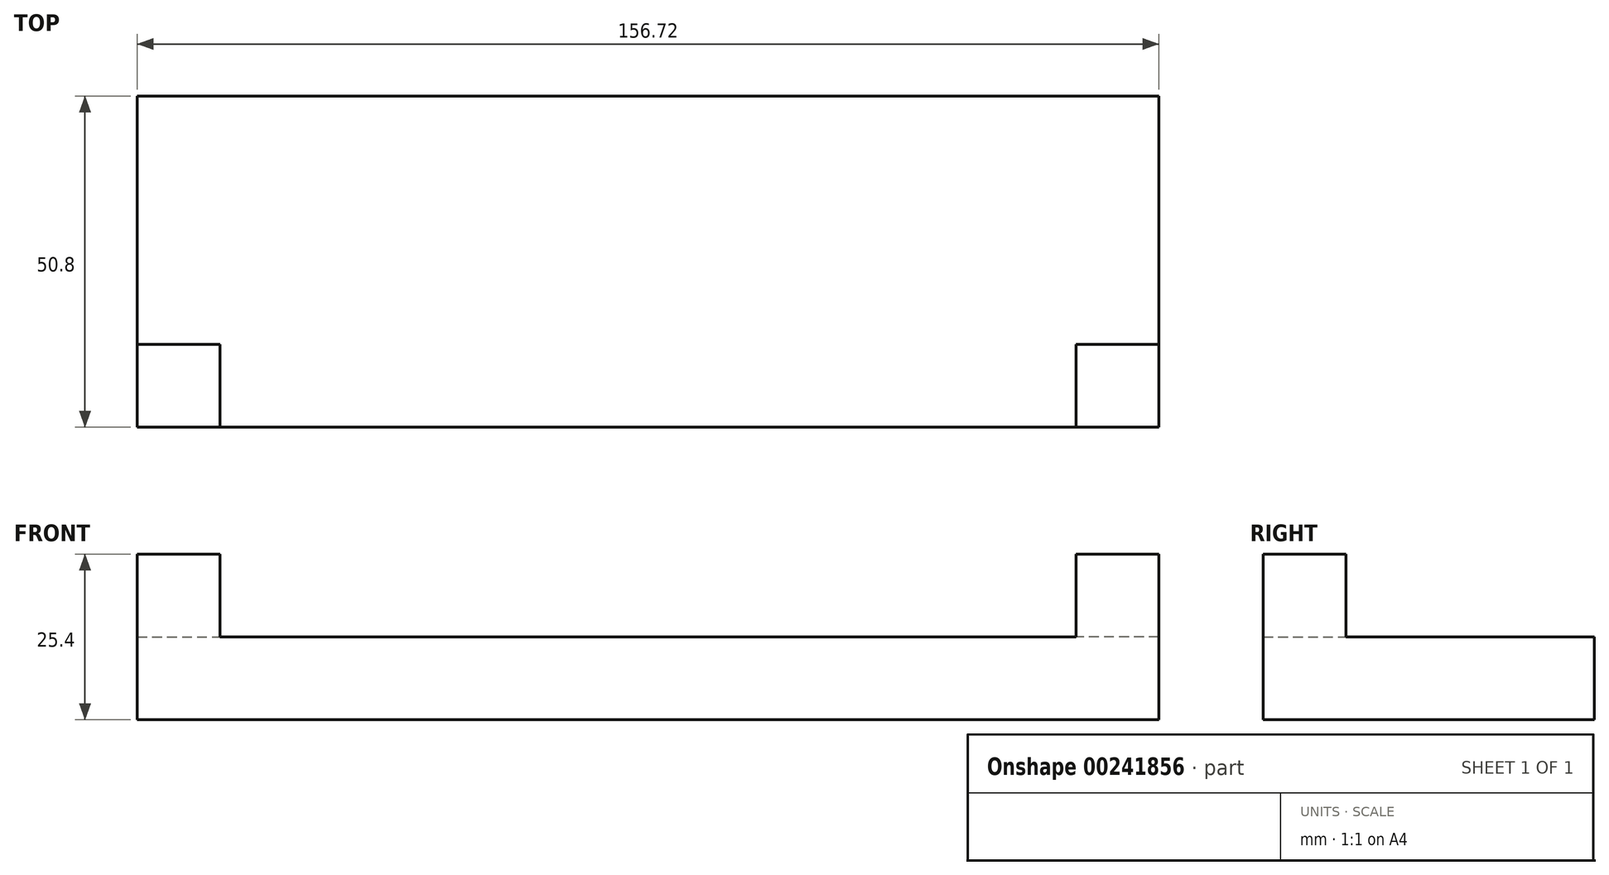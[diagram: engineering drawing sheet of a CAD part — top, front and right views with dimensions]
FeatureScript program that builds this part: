
annotation { "Feature Type Name" : "Feature", "Feature Type Description" : "" }
export const myFeature = defineFeature(function(context is Context, id is Id, definition is map)
    precondition{}
    {
        {
            var Q0;
            Q0=qCreatedBy(makeId("Top.planeOp"),FACE);
            var sketch = newSketch(context, id + "F0", { "sketchPlane" : qUnion([Q0])});
            skLineSegment(sketch, "E0.bottom", {"start": v(-78.36, 25.4) * mm, "end": v(78.36, 25.4) * mm});
            skLineSegment(sketch, "E0.top", {"start": v(-78.36, -25.4) * mm, "end": v(78.36, -25.4) * mm});
            skLineSegment(sketch, "E0.left", {"start": v(-78.36, 25.4) * mm, "end": v(-78.36, -25.4) * mm});
            skLineSegment(sketch, "E0.right", {"start": v(78.36, 25.4) * mm, "end": v(78.36, -25.4) * mm});
            skPoint(sketch, "E0.middle", {"position": v(0, 0) * mm});
            skSolve(sketch);
        }
        {
            var Q0;
            Q0 = qSketchRegion(id + "F0", true);
            extrude(context, id + "F1", {"entities" : qUnion([Q0]), "depth" : 12.7 * mm});
        }
        {
            var Q0;
            Q0=makeQuery(id+"F1.opExtrude","CAP_FACE",FACE,{"disambiguationData":[OSD([sQuery(id+"F0.wireOp",EDGE,"E0.bottom"),sQuery(id+"F0.wireOp",EDGE,"E0.top"),sQuery(id+"F0.wireOp",EDGE,"E0.left"),sQuery(id+"F0.wireOp",EDGE,"E0.right")])],"isStart":false});
            var sketch = newSketch(context, id + "F2", { "sketchPlane" : qUnion([Q0])});
            skLineSegment(sketch, "E1.bottom", {"start": v(-78.36, -25.4) * mm, "end": v(-65.66, -25.4) * mm});
            skLineSegment(sketch, "E1.top", {"start": v(-78.36, -12.7) * mm, "end": v(-65.66, -12.7) * mm});
            skLineSegment(sketch, "E1.left", {"start": v(-78.36, -25.4) * mm, "end": v(-78.36, -12.7) * mm});
            skLineSegment(sketch, "E1.right", {"start": v(-65.66, -25.4) * mm, "end": v(-65.66, -12.7) * mm});
            skSolve(sketch);
        }
        {
            var Q0;
            Q0 = qSketchRegion(id + "F2", true);
            extrude(context, id + "F3", {"entities" : qUnion([Q0]), "operationType" : NewBodyOperationType.ADD, "depth" : 12.7 * mm});
        }
        {
            var Q0;
            Q0=makeQuery(id+"F1.opExtrude","CAP_FACE",FACE,{"disambiguationData":[OSD([sQuery(id+"F0.wireOp",EDGE,"E0.bottom"),sQuery(id+"F0.wireOp",EDGE,"E0.top"),sQuery(id+"F0.wireOp",EDGE,"E0.left"),sQuery(id+"F0.wireOp",EDGE,"E0.right")])],"isStart":false});
            var sketch = newSketch(context, id + "F4", { "sketchPlane" : qUnion([Q0])});
            skLineSegment(sketch, "E2.bottom", {"start": v(78.36, -25.4) * mm, "end": v(65.66, -25.4) * mm});
            skLineSegment(sketch, "E2.top", {"start": v(78.36, -12.7) * mm, "end": v(65.66, -12.7) * mm});
            skLineSegment(sketch, "E2.left", {"start": v(78.36, -25.4) * mm, "end": v(78.36, -12.7) * mm});
            skLineSegment(sketch, "E2.right", {"start": v(65.66, -25.4) * mm, "end": v(65.66, -12.7) * mm});
            skSolve(sketch);
        }
        {
            var Q0;
            Q0 = qSketchRegion(id + "F4", true);
            extrude(context, id + "F5", {"entities" : qUnion([Q0]), "operationType" : NewBodyOperationType.ADD, "depth" : 12.7 * mm});
        }
    });
